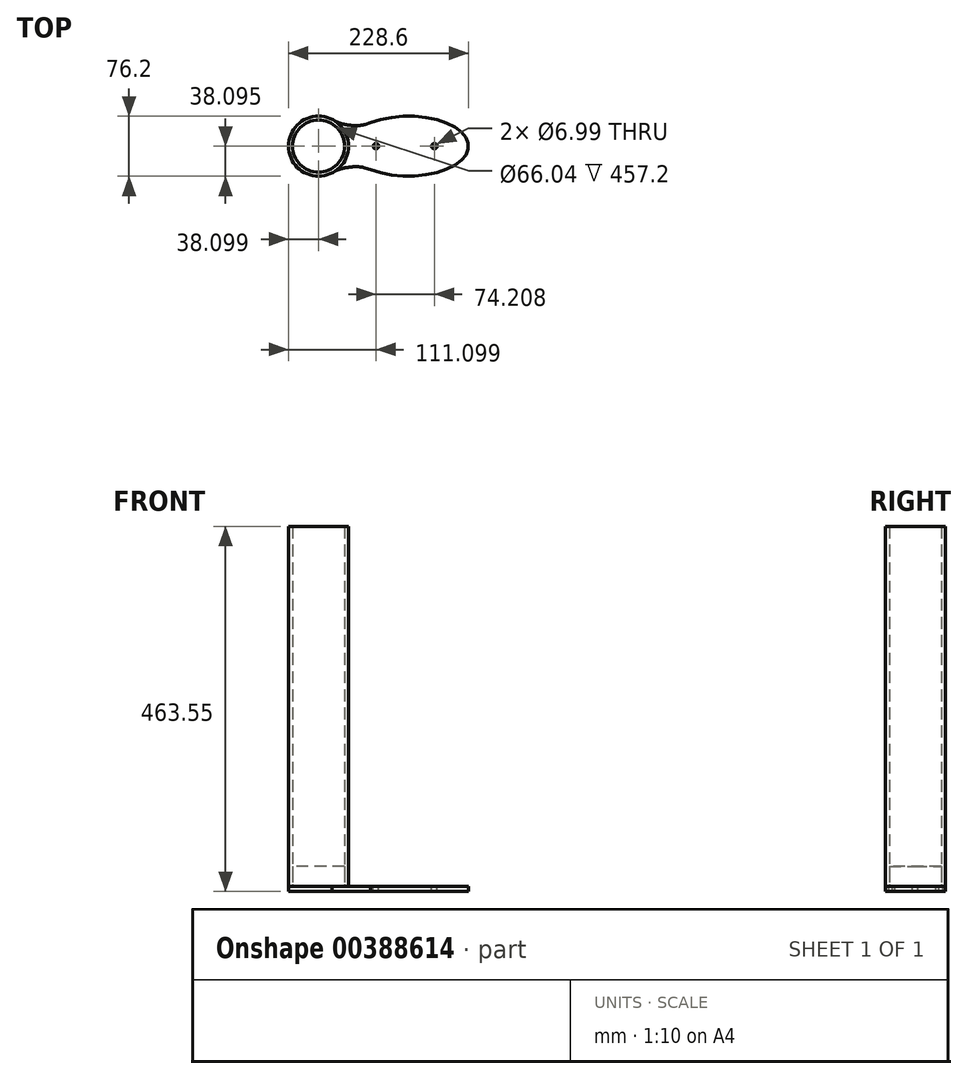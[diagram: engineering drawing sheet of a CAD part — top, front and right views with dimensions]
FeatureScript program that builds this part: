
annotation { "Feature Type Name" : "Feature", "Feature Type Description" : "" }
export const myFeature = defineFeature(function(context is Context, id is Id, definition is map)
    precondition{}
    {
        {
            var Q0;
            Q0=qCreatedBy(makeId("Top.planeOp"),FACE);
            var sketch = newSketch(context, id + "F0", { "sketchPlane" : qUnion([Q0])});
            skCircle(sketch, "E0", {"center": v(10.04, 46.65) * mm, "radius": 38.1 * mm});
            skEllipse(sketch, "E1", {"center": v(124.34, 46.65) * mm, "majorRadius": 76.2 * mm, "minorRadius": 38.1 * mm, "majorAxis": v(1, 0)});
            skLineSegment(sketch, "E2", {"start": v(48.14, 46.65) * mm, "end": v(48.14, 46.65) * mm});
            skLineSegment(sketch, "E3.bottom", {"start": v(10.04, 46.65) * mm, "end": v(48.14, 46.65) * mm});
            skLineSegment(sketch, "E3.top", {"start": v(10.04, 68.24) * mm, "end": v(48.14, 68.24) * mm});
            skLineSegment(sketch, "E3.left", {"start": v(10.04, 46.65) * mm, "end": v(10.04, 68.24) * mm});
            skLineSegment(sketch, "E3.right", {"start": v(48.14, 46.65) * mm, "end": v(48.14, 68.24) * mm});
            skLineSegment(sketch, "E4.top", {"start": v(10.04, 25.06) * mm, "end": v(48.14, 25.06) * mm});
            skLineSegment(sketch, "E4.left", {"start": v(10.04, 46.65) * mm, "end": v(10.04, 25.06) * mm});
            skLineSegment(sketch, "E4.right", {"start": v(48.14, 46.65) * mm, "end": v(48.14, 25.06) * mm});
            skLineSegment(sketch, "E5", {"start": v(48.14, 68.24) * mm, "end": v(76.44, 76.28) * mm});
            skLineSegment(sketch, "E6", {"start": v(76.44, 76.28) * mm, "end": v(76.44, 17.01) * mm});
            skLineSegment(sketch, "E7", {"start": v(76.44, 17.01) * mm, "end": v(48.14, 25.06) * mm});
            skLineSegment(sketch, "E8", {"start": v(48.14, 68.24) * mm, "end": v(26.92, 80.8) * mm});
            skLineSegment(sketch, "E9", {"start": v(26.92, 80.8) * mm, "end": v(26.92, 12.49) * mm});
            skLineSegment(sketch, "E10", {"start": v(26.92, 12.49) * mm, "end": v(48.14, 25.06) * mm});
            skSolve(sketch);
        }
        {
            var Q0;
            {var subQ0=sQuery(id+"F0.wireOp",EDGE,"E8");var subQ1=sQuery(id+"F0.wireOp",EDGE,"E0");var subQ2=makeQuery(id+"F0.imprint","INTERSECT",VERTEX,{"derivedFrom":[subQ1,subQ0]});Q0=makeQuery(id+"F0.imprint","IMPRINT",FACE,{"disambiguationData":[TD([[makeQuery(id+"F0.imprint","IMPRINT",EDGE,{"disambiguationData":[TD([[subQ2,1.0]])],"derivedFrom":subQ1}),-1.0]])]});}
            var Q1;
            {var subQ0=sQuery(id+"F0.wireOp",EDGE,"E8");var subQ1=sQuery(id+"F0.wireOp",EDGE,"E0");var subQ2=makeQuery(id+"F0.imprint","INTERSECT",VERTEX,{"derivedFrom":[subQ1,subQ0]});Q1=makeQuery(id+"F0.imprint","IMPRINT",FACE,{"disambiguationData":[TD([[makeQuery(id+"F0.imprint","IMPRINT",EDGE,{"disambiguationData":[TD([[subQ2,1.0]])],"derivedFrom":subQ1}),1.0]])]});}
            var Q2;
            {var subQ0=sQuery(id+"F0.wireOp",EDGE,"E3.left");Q2=makeQuery(id+"F0.imprint","IMPRINT",FACE,{"disambiguationData":[TD([[makeQuery(id+"F0.imprint","IMPRINT",EDGE,{"derivedFrom":subQ0}),-1.0]])]});}
            var Q3;
            {var subQ0=sQuery(id+"F0.wireOp",EDGE,"E4.left");Q3=makeQuery(id+"F0.imprint","IMPRINT",FACE,{"disambiguationData":[TD([[makeQuery(id+"F0.imprint","IMPRINT",EDGE,{"derivedFrom":subQ0}),1.0]])]});}
            var Q4;
            {var subQ0=sQuery(id+"F0.wireOp",EDGE,"E10");var subQ1=sQuery(id+"F0.wireOp",EDGE,"E0");var subQ2=makeQuery(id+"F0.imprint","INTERSECT",VERTEX,{"derivedFrom":[subQ1,subQ0]});Q4=makeQuery(id+"F0.imprint","IMPRINT",FACE,{"disambiguationData":[TD([[makeQuery(id+"F0.imprint","IMPRINT",EDGE,{"disambiguationData":[TD([[subQ2,-1.0]])],"derivedFrom":subQ1}),-1.0]])]});}
            var Q5;
            {var subQ0=sQuery(id+"F0.wireOp",EDGE,"E10");var subQ1=sQuery(id+"F0.wireOp",EDGE,"E0");var subQ2=makeQuery(id+"F0.imprint","INTERSECT",VERTEX,{"derivedFrom":[subQ1,subQ0]});Q5=makeQuery(id+"F0.imprint","IMPRINT",FACE,{"disambiguationData":[TD([[makeQuery(id+"F0.imprint","IMPRINT",EDGE,{"disambiguationData":[TD([[subQ2,-1.0]])],"derivedFrom":subQ1}),1.0]])]});}
            var Q6;
            {var subQ1=sQuery(id+"F0.wireOp",EDGE,"E0");var subQ3=sQuery(id+"F0.wireOp",EDGE,"E4.top");var subQ4=makeQuery(id+"F0.imprint","INTERSECT",VERTEX,{"derivedFrom":[subQ1,subQ3]});Q6=makeQuery(id+"F0.imprint","IMPRINT",FACE,{"disambiguationData":[TD([[makeQuery(id+"F0.imprint","IMPRINT",EDGE,{"disambiguationData":[TD([[subQ4,1.0]])],"derivedFrom":subQ3}),1.0]])]});}
            var Q7;
            {var subQ1=sQuery(id+"F0.wireOp",EDGE,"E0");var subQ3=sQuery(id+"F0.wireOp",EDGE,"E3.top");var subQ4=makeQuery(id+"F0.imprint","INTERSECT",VERTEX,{"derivedFrom":[subQ1,subQ3]});Q7=makeQuery(id+"F0.imprint","IMPRINT",FACE,{"disambiguationData":[TD([[makeQuery(id+"F0.imprint","IMPRINT",EDGE,{"disambiguationData":[TD([[subQ4,1.0]])],"derivedFrom":subQ3}),-1.0]])]});}
            var Q8;
            {var subQ0=sQuery(id+"F0.wireOp",EDGE,"E3.right");Q8=makeQuery(id+"F0.imprint","IMPRINT",FACE,{"disambiguationData":[TD([[makeQuery(id+"F0.imprint","IMPRINT",EDGE,{"derivedFrom":subQ0}),1.0]])]});}
            var Q9;
            {var subQ0=sQuery(id+"F0.wireOp",EDGE,"E4.right");Q9=makeQuery(id+"F0.imprint","IMPRINT",FACE,{"disambiguationData":[TD([[makeQuery(id+"F0.imprint","IMPRINT",EDGE,{"derivedFrom":subQ0}),-1.0]])]});}
            var Q10;
            {var subQ0=sQuery(id+"F0.wireOp",EDGE,"E4.right");Q10=makeQuery(id+"F0.imprint","IMPRINT",FACE,{"disambiguationData":[TD([[makeQuery(id+"F0.imprint","IMPRINT",EDGE,{"derivedFrom":subQ0}),1.0]])]});}
            var Q11;
            {var subQ0=sQuery(id+"F0.wireOp",EDGE,"E3.right");Q11=makeQuery(id+"F0.imprint","IMPRINT",FACE,{"disambiguationData":[TD([[makeQuery(id+"F0.imprint","IMPRINT",EDGE,{"derivedFrom":subQ0}),-1.0]])]});}
            var Q12;
            {var subQ2=sQuery(id+"F0.wireOp",EDGE,"E6");Q12=makeQuery(id+"F0.imprint","IMPRINT",FACE,{"disambiguationData":[TD([[makeQuery(id+"F0.imprint","IMPRINT",EDGE,{"derivedFrom":subQ2}),-1.0]])]});}
            var Q13;
            {var subQ0=sQuery(id+"F0.wireOp",EDGE,"E6");Q13=makeQuery(id+"F0.imprint","IMPRINT",FACE,{"disambiguationData":[TD([[makeQuery(id+"F0.imprint","IMPRINT",EDGE,{"derivedFrom":subQ0}),1.0]])]});}
            var Q14;
            {var subQ4=sQuery(id+"F0.wireOp",EDGE,"E3.left");Q14=makeQuery(id+"F0.imprint","IMPRINT",FACE,{"disambiguationData":[TD([[makeQuery(id+"F0.imprint","IMPRINT",EDGE,{"derivedFrom":subQ4}),1.0]])]});}
            extrude(context, id + "F1", {"entities" : qUnion([Q0, Q1, Q2, Q3, Q4, Q5, Q6, Q7, Q8, Q9, Q10, Q11, Q12, Q13, Q14]), "depth" : 6.35 * mm});
        }
        {
            var Q0;
            Q0=makeQuery(id+"F1.opExtrude","SWEPT_EDGE",EDGE,{"disambiguationData":[OSD([sQuery(id+"F0.wireOp",EDGE,"E4.top"),sQuery(id+"F0.wireOp",EDGE,"E4.right"),sQuery(id+"F0.wireOp",EDGE,"E7"),sQuery(id+"F0.wireOp",EDGE,"E10")])]});
            fillet(context, id + "F2", {"entities" : qUnion([Q0]), "radius" : 50.8 * mm, "tangentPropagation" : true, "rho" : .4, "crossSection" : FilletCrossSection.CONIC, "allowEdgeOverflow" : false});
        }
        {
            var Q0;
            Q0=makeQuery(id+"F1.opExtrude","SWEPT_EDGE",EDGE,{"disambiguationData":[OSD([sQuery(id+"F0.wireOp",EDGE,"E3.top"),sQuery(id+"F0.wireOp",EDGE,"E3.right"),sQuery(id+"F0.wireOp",EDGE,"E5"),sQuery(id+"F0.wireOp",EDGE,"E8")])]});
            fillet(context, id + "F3", {"entities" : qUnion([Q0]), "radius" : 50.8 * mm, "tangentPropagation" : true, "rho" : .4, "crossSection" : FilletCrossSection.CONIC, "allowEdgeOverflow" : false});
        }
        {
            var Q0;
            Q0=makeQuery(id+"F1.opExtrude","CAP_FACE",FACE,{"disambiguationData":[OSD([sQuery(id+"F0.wireOp",EDGE,"E0"),sQuery(id+"F0.wireOp",EDGE,"E1"),sQuery(id+"F0.wireOp",EDGE,"E5"),sQuery(id+"F0.wireOp",EDGE,"E7"),sQuery(id+"F0.wireOp",EDGE,"E8"),sQuery(id+"F0.wireOp",EDGE,"E10")])],"isStart":false});
            var sketch = newSketch(context, id + "F4", { "sketchPlane" : qUnion([Q0])});
            skCircle(sketch, "E11", {"center": v(157.25, 46.65) * mm, "radius": 3.5 * mm});
            skPoint(sketch, "E11.centerSnap0", {"position": v(200.54, 46.65) * mm});
            skCircle(sketch, "E12", {"center": v(83.04, 46.65) * mm, "radius": 3.5 * mm});
            skSolve(sketch);
        }
        {
            var Q0;
            Q0=makeQuery(id+"F4.imprint","IMPRINT",FACE,{"disambiguationData":[TD([[makeQuery(id+"F4.imprint","IMPRINT",EDGE,{"derivedFrom":sQuery(id+"F4.wireOp",EDGE,"E12")}),1.0]])]});
            var Q1;
            Q1=makeQuery(id+"F4.imprint","IMPRINT",FACE,{"disambiguationData":[TD([[makeQuery(id+"F4.imprint","IMPRINT",EDGE,{"derivedFrom":sQuery(id+"F4.wireOp",EDGE,"E11")}),1.0]])]});
            extrude(context, id + "F5", {"entities" : qUnion([Q0, Q1]), "operationType" : NewBodyOperationType.REMOVE, "endBound" : BoundingType.THROUGH_ALL, "oppositeDirection" : true, "depth" : 25.4 * mm});
        }
        {
            var Q0;
            Q0=makeQuery(id+"F1.opExtrude","CAP_FACE",FACE,{"disambiguationData":[OSD([sQuery(id+"F0.wireOp",EDGE,"E0"),sQuery(id+"F0.wireOp",EDGE,"E1"),sQuery(id+"F0.wireOp",EDGE,"E5"),sQuery(id+"F0.wireOp",EDGE,"E7"),sQuery(id+"F0.wireOp",EDGE,"E8"),sQuery(id+"F0.wireOp",EDGE,"E10")])],"isStart":false});
            var sketch = newSketch(context, id + "F6", { "sketchPlane" : qUnion([Q0])});
            skCircle(sketch, "E13", {"center": v(10.04, 46.65) * mm, "radius": 38.1 * mm});
            skCircle(sketch, "E14", {"center": v(10.04, 46.65) * mm, "radius": 33.02 * mm});
            skSolve(sketch);
        }
        {
            var Q0;
            Q0=makeQuery(id+"F6.imprint","IMPRINT",FACE,{"disambiguationData":[TD([[makeQuery(id+"F6.imprint","IMPRINT",EDGE,{"derivedFrom":sQuery(id+"F6.wireOp",EDGE,"E14")}),-1.0]])]});
            var Q1;
            {var subQ1=sQuery(id+"F0.wireOp",EDGE,"E8");var subQ2=makeQuery(id+"F1.opExtrude","CAP_EDGE",EDGE,{"disambiguationData":[OSD([subQ1])],"isStart":false});Q1=makeQuery(id+"F6.imprint","IMPRINT",FACE,{"disambiguationData":[TD([[makeQuery(id+"F6.imprint","IMPRINT",EDGE,{"derivedFrom":subQ2}),-1.0]])]});}
            var Q2;
            {var subQ1=sQuery(id+"F0.wireOp",EDGE,"E10");var subQ2=makeQuery(id+"F1.opExtrude","CAP_EDGE",EDGE,{"disambiguationData":[OSD([subQ1])],"isStart":false});Q2=makeQuery(id+"F6.imprint","IMPRINT",FACE,{"disambiguationData":[TD([[makeQuery(id+"F6.imprint","IMPRINT",EDGE,{"derivedFrom":subQ2}),-1.0]])]});}
            extrude(context, id + "F7", {"entities" : qUnion([Q0, Q1, Q2]), "depth" : 457.2 * mm});
        }
        {
            var Q0;
            Q0=makeQuery(id+"F6.imprint","IMPRINT",FACE,{"disambiguationData":[TD([[makeQuery(id+"F6.imprint","IMPRINT",EDGE,{"derivedFrom":sQuery(id+"F6.wireOp",EDGE,"E14")}),1.0]])]});
            extrude(context, id + "F8", {"entities" : qUnion([Q0]), "depth" : 25.4 * mm});
        }
    });
